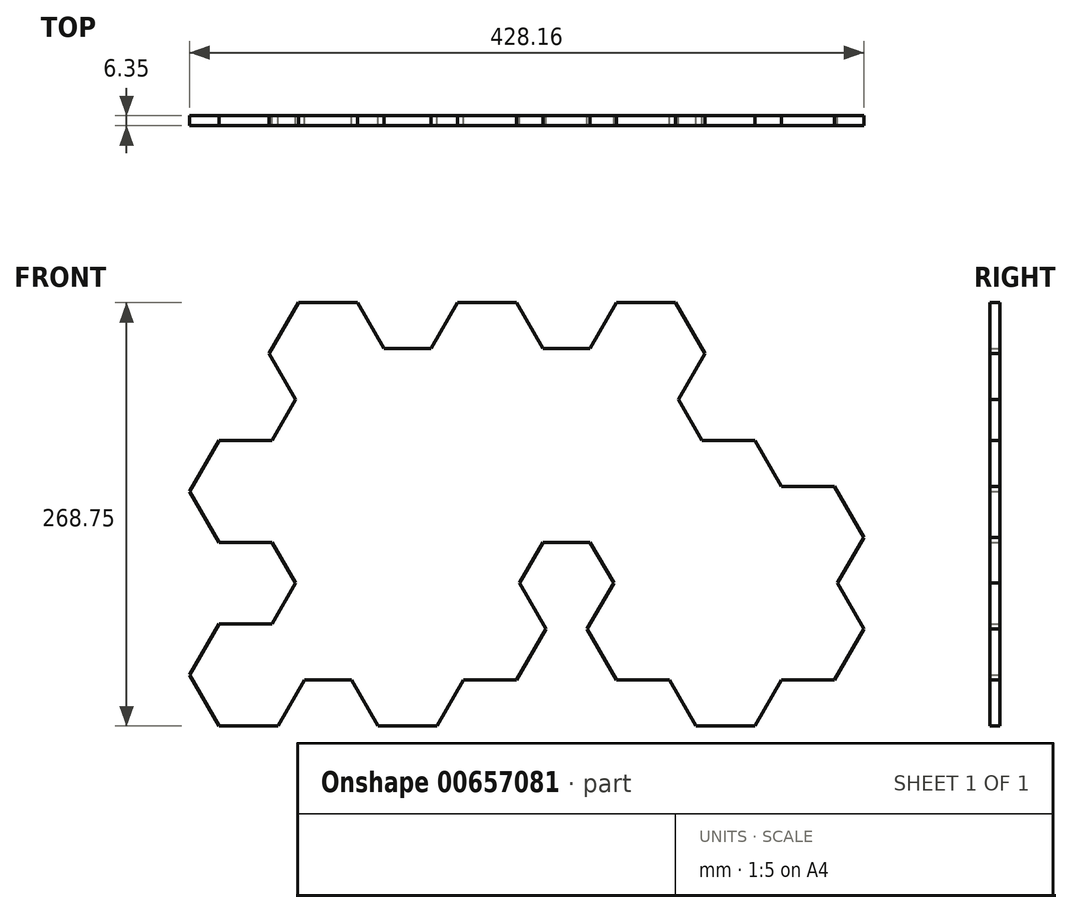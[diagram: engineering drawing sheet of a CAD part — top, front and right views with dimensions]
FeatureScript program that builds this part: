
annotation { "Feature Type Name" : "Feature", "Feature Type Description" : "" }
export const myFeature = defineFeature(function(context is Context, id is Id, definition is map)
    precondition{}
    {
        {
            var Q0;
            Q0=qCreatedBy(makeId("Front.planeOp"),FACE);
            var sketch = newSketch(context, id + "F0", { "sketchPlane" : qUnion([Q0])});
            skCircle(sketch, "E0.cCircle", {"center": v(-7.98, -23.48) * mm, "radius": 25.98 * mm, "construction": true});
            skLineSegment(sketch, "E0.0", {"start": v(22.02, -23.48) * mm, "end": v(7.02, -49.46) * mm});
            skLineSegment(sketch, "E0.1", {"start": v(7.02, -49.46) * mm, "end": v(-22.98, -49.46) * mm});
            skLineSegment(sketch, "E0.2", {"start": v(-22.98, -49.46) * mm, "end": v(-37.98, -23.48) * mm});
            skLineSegment(sketch, "E0.3", {"start": v(-37.98, -23.48) * mm, "end": v(-22.98, 2.5) * mm});
            skLineSegment(sketch, "E0.4", {"start": v(-22.98, 2.5) * mm, "end": v(7.02, 2.5) * mm});
            skLineSegment(sketch, "E0.5", {"start": v(7.02, 2.5) * mm, "end": v(22.02, -23.48) * mm});
            skPoint(sketch, "E0.0.midPoint", {"position": v(14.52, -36.47) * mm});
            skCircle(sketch, "E1.cCircle", {"center": v(-7.98, -81.8) * mm, "radius": 25.98 * mm, "construction": true});
            skLineSegment(sketch, "E1.0", {"start": v(22.02, -81.8) * mm, "end": v(7.02, -107.77) * mm});
            skLineSegment(sketch, "E1.1", {"start": v(7.02, -107.77) * mm, "end": v(-22.98, -107.77) * mm});
            skLineSegment(sketch, "E1.2", {"start": v(-22.98, -107.77) * mm, "end": v(-37.98, -81.8) * mm});
            skLineSegment(sketch, "E1.3", {"start": v(-37.98, -81.8) * mm, "end": v(-22.98, -55.81) * mm});
            skLineSegment(sketch, "E1.4", {"start": v(-22.98, -55.81) * mm, "end": v(7.02, -55.81) * mm});
            skLineSegment(sketch, "E1.5", {"start": v(7.02, -55.81) * mm, "end": v(22.02, -81.8) * mm});
            skPoint(sketch, "E1.0.midPoint", {"position": v(14.52, -94.78) * mm});
            skCircle(sketch, "E2.cCircle", {"center": v(-108.98, -81.8) * mm, "radius": 25.98 * mm, "construction": true});
            skLineSegment(sketch, "E2.0", {"start": v(-78.98, -81.8) * mm, "end": v(-93.98, -107.77) * mm});
            skLineSegment(sketch, "E2.1", {"start": v(-93.98, -107.77) * mm, "end": v(-123.98, -107.77) * mm});
            skLineSegment(sketch, "E2.2", {"start": v(-123.98, -107.77) * mm, "end": v(-138.98, -81.8) * mm});
            skLineSegment(sketch, "E2.3", {"start": v(-138.98, -81.8) * mm, "end": v(-123.98, -55.81) * mm});
            skLineSegment(sketch, "E2.4", {"start": v(-123.98, -55.81) * mm, "end": v(-93.98, -55.81) * mm});
            skLineSegment(sketch, "E2.5", {"start": v(-93.98, -55.81) * mm, "end": v(-78.98, -81.8) * mm});
            skPoint(sketch, "E2.0.midPoint", {"position": v(-86.48, -94.78) * mm});
            skCircle(sketch, "E3.cCircle", {"center": v(-108.98, -23.48) * mm, "radius": 25.98 * mm, "construction": true});
            skLineSegment(sketch, "E3.0", {"start": v(-78.98, -23.48) * mm, "end": v(-93.98, -49.46) * mm});
            skLineSegment(sketch, "E3.1", {"start": v(-93.98, -49.46) * mm, "end": v(-123.98, -49.46) * mm});
            skLineSegment(sketch, "E3.2", {"start": v(-123.98, -49.46) * mm, "end": v(-138.98, -23.48) * mm});
            skLineSegment(sketch, "E3.3", {"start": v(-138.98, -23.48) * mm, "end": v(-123.98, 2.5) * mm});
            skLineSegment(sketch, "E3.4", {"start": v(-123.98, 2.5) * mm, "end": v(-93.98, 2.5) * mm});
            skLineSegment(sketch, "E3.5", {"start": v(-93.98, 2.5) * mm, "end": v(-78.98, -23.48) * mm});
            skPoint(sketch, "E3.0.midPoint", {"position": v(-86.48, -36.47) * mm});
            skCircle(sketch, "E4.cCircle", {"center": v(-58.48, 5.67) * mm, "radius": 25.98 * mm, "construction": true});
            skLineSegment(sketch, "E4.0", {"start": v(-28.48, 5.67) * mm, "end": v(-43.48, -20.3) * mm});
            skLineSegment(sketch, "E4.1", {"start": v(-43.48, -20.3) * mm, "end": v(-73.48, -20.3) * mm});
            skLineSegment(sketch, "E4.2", {"start": v(-73.48, -20.3) * mm, "end": v(-88.48, 5.67) * mm});
            skLineSegment(sketch, "E4.3", {"start": v(-88.48, 5.67) * mm, "end": v(-73.48, 31.65) * mm});
            skLineSegment(sketch, "E4.4", {"start": v(-73.48, 31.65) * mm, "end": v(-43.48, 31.65) * mm});
            skLineSegment(sketch, "E4.5", {"start": v(-43.48, 31.65) * mm, "end": v(-28.48, 5.67) * mm});
            skPoint(sketch, "E4.0.midPoint", {"position": v(-35.98, -7.32) * mm});
            skCircle(sketch, "E5.cCircle", {"center": v(42.52, -110.95) * mm, "radius": 25.98 * mm, "construction": true});
            skLineSegment(sketch, "E5.0", {"start": v(72.52, -110.95) * mm, "end": v(57.52, -136.93) * mm});
            skLineSegment(sketch, "E5.1", {"start": v(57.52, -136.93) * mm, "end": v(27.52, -136.93) * mm});
            skLineSegment(sketch, "E5.2", {"start": v(27.52, -136.93) * mm, "end": v(12.52, -110.95) * mm});
            skLineSegment(sketch, "E5.3", {"start": v(12.52, -110.95) * mm, "end": v(27.52, -84.97) * mm});
            skLineSegment(sketch, "E5.4", {"start": v(27.52, -84.97) * mm, "end": v(57.52, -84.97) * mm});
            skLineSegment(sketch, "E5.5", {"start": v(57.52, -84.97) * mm, "end": v(72.52, -110.95) * mm});
            skPoint(sketch, "E5.0.midPoint", {"position": v(65.02, -123.94) * mm});
            skCircle(sketch, "E6.cCircle", {"center": v(-159.48, -110.95) * mm, "radius": 25.98 * mm, "construction": true});
            skLineSegment(sketch, "E6.0", {"start": v(-129.48, -110.95) * mm, "end": v(-144.48, -136.93) * mm});
            skLineSegment(sketch, "E6.1", {"start": v(-144.48, -136.93) * mm, "end": v(-174.48, -136.93) * mm});
            skLineSegment(sketch, "E6.2", {"start": v(-174.48, -136.93) * mm, "end": v(-189.48, -110.95) * mm});
            skLineSegment(sketch, "E6.3", {"start": v(-189.48, -110.95) * mm, "end": v(-174.48, -84.97) * mm});
            skLineSegment(sketch, "E6.4", {"start": v(-174.48, -84.97) * mm, "end": v(-144.48, -84.97) * mm});
            skLineSegment(sketch, "E6.5", {"start": v(-144.48, -84.97) * mm, "end": v(-129.48, -110.95) * mm});
            skPoint(sketch, "E6.0.midPoint", {"position": v(-136.98, -123.94) * mm});
            skCircle(sketch, "E7.cCircle", {"center": v(42.52, -52.64) * mm, "radius": 25.98 * mm, "construction": true});
            skLineSegment(sketch, "E7.0", {"start": v(72.52, -52.64) * mm, "end": v(57.52, -78.62) * mm});
            skLineSegment(sketch, "E7.1", {"start": v(57.52, -78.62) * mm, "end": v(27.52, -78.62) * mm});
            skLineSegment(sketch, "E7.2", {"start": v(27.52, -78.62) * mm, "end": v(12.52, -52.64) * mm});
            skLineSegment(sketch, "E7.3", {"start": v(12.52, -52.64) * mm, "end": v(27.52, -26.66) * mm});
            skLineSegment(sketch, "E7.4", {"start": v(27.52, -26.66) * mm, "end": v(57.52, -26.66) * mm});
            skLineSegment(sketch, "E7.5", {"start": v(57.52, -26.66) * mm, "end": v(72.52, -52.64) * mm});
            skPoint(sketch, "E7.0.midPoint", {"position": v(65.02, -65.63) * mm});
            skCircle(sketch, "E8.cCircle", {"center": v(93.02, -81.8) * mm, "radius": 25.98 * mm, "construction": true});
            skLineSegment(sketch, "E8.0", {"start": v(123.02, -81.8) * mm, "end": v(108.02, -107.77) * mm});
            skLineSegment(sketch, "E8.1", {"start": v(108.02, -107.77) * mm, "end": v(78.02, -107.77) * mm});
            skLineSegment(sketch, "E8.2", {"start": v(78.02, -107.77) * mm, "end": v(63.02, -81.8) * mm});
            skLineSegment(sketch, "E8.3", {"start": v(63.02, -81.8) * mm, "end": v(78.02, -55.81) * mm});
            skLineSegment(sketch, "E8.4", {"start": v(78.02, -55.81) * mm, "end": v(108.02, -55.81) * mm});
            skLineSegment(sketch, "E8.5", {"start": v(108.02, -55.81) * mm, "end": v(123.02, -81.8) * mm});
            skPoint(sketch, "E8.0.midPoint", {"position": v(115.52, -94.78) * mm});
            skCircle(sketch, "E9.cCircle", {"center": v(93.02, -23.48) * mm, "radius": 25.98 * mm, "construction": true});
            skLineSegment(sketch, "E9.0", {"start": v(123.02, -23.48) * mm, "end": v(108.02, -49.46) * mm});
            skLineSegment(sketch, "E9.1", {"start": v(108.02, -49.46) * mm, "end": v(78.02, -49.46) * mm});
            skLineSegment(sketch, "E9.2", {"start": v(78.02, -49.46) * mm, "end": v(63.02, -23.48) * mm});
            skLineSegment(sketch, "E9.3", {"start": v(63.02, -23.48) * mm, "end": v(78.02, 2.5) * mm});
            skLineSegment(sketch, "E9.4", {"start": v(78.02, 2.5) * mm, "end": v(108.02, 2.5) * mm});
            skLineSegment(sketch, "E9.5", {"start": v(108.02, 2.5) * mm, "end": v(123.02, -23.48) * mm});
            skPoint(sketch, "E9.0.midPoint", {"position": v(115.52, -36.47) * mm});
            skCircle(sketch, "E10.cCircle", {"center": v(42.52, 5.67) * mm, "radius": 25.98 * mm, "construction": true});
            skLineSegment(sketch, "E10.0", {"start": v(72.52, 5.67) * mm, "end": v(57.52, -20.3) * mm});
            skLineSegment(sketch, "E10.1", {"start": v(57.52, -20.3) * mm, "end": v(27.52, -20.3) * mm});
            skLineSegment(sketch, "E10.2", {"start": v(27.52, -20.3) * mm, "end": v(12.52, 5.67) * mm});
            skLineSegment(sketch, "E10.3", {"start": v(12.52, 5.67) * mm, "end": v(27.52, 31.65) * mm});
            skLineSegment(sketch, "E10.4", {"start": v(27.52, 31.65) * mm, "end": v(57.52, 31.65) * mm});
            skLineSegment(sketch, "E10.5", {"start": v(57.52, 31.65) * mm, "end": v(72.52, 5.67) * mm});
            skPoint(sketch, "E10.0.midPoint", {"position": v(65.02, -7.32) * mm});
            skCircle(sketch, "E11.cCircle", {"center": v(-7.98, 34.83) * mm, "radius": 25.98 * mm, "construction": true});
            skLineSegment(sketch, "E11.0", {"start": v(22.02, 34.83) * mm, "end": v(7.02, 8.85) * mm});
            skLineSegment(sketch, "E11.1", {"start": v(7.02, 8.85) * mm, "end": v(-22.98, 8.85) * mm});
            skLineSegment(sketch, "E11.2", {"start": v(-22.98, 8.85) * mm, "end": v(-37.98, 34.83) * mm});
            skLineSegment(sketch, "E11.3", {"start": v(-37.98, 34.83) * mm, "end": v(-22.98, 60.81) * mm});
            skLineSegment(sketch, "E11.4", {"start": v(-22.98, 60.81) * mm, "end": v(7.02, 60.81) * mm});
            skLineSegment(sketch, "E11.5", {"start": v(7.02, 60.81) * mm, "end": v(22.02, 34.83) * mm});
            skPoint(sketch, "E11.0.midPoint", {"position": v(14.52, 21.84) * mm});
            skCircle(sketch, "E12.cCircle", {"center": v(-7.98, 93.14) * mm, "radius": 25.98 * mm, "construction": true});
            skLineSegment(sketch, "E12.0", {"start": v(22.02, 93.14) * mm, "end": v(7.02, 67.16) * mm});
            skLineSegment(sketch, "E12.1", {"start": v(7.02, 67.16) * mm, "end": v(-22.98, 67.16) * mm});
            skLineSegment(sketch, "E12.2", {"start": v(-22.98, 67.16) * mm, "end": v(-37.98, 93.14) * mm});
            skLineSegment(sketch, "E12.3", {"start": v(-37.98, 93.14) * mm, "end": v(-22.98, 119.12) * mm});
            skLineSegment(sketch, "E12.4", {"start": v(-22.98, 119.12) * mm, "end": v(7.02, 119.12) * mm});
            skLineSegment(sketch, "E12.5", {"start": v(7.02, 119.12) * mm, "end": v(22.02, 93.14) * mm});
            skPoint(sketch, "E12.0.midPoint", {"position": v(14.52, 80.15) * mm});
            skCircle(sketch, "E13.cCircle", {"center": v(-58.48, 63.99) * mm, "radius": 25.98 * mm, "construction": true});
            skLineSegment(sketch, "E13.0", {"start": v(-28.48, 63.99) * mm, "end": v(-43.48, 38) * mm});
            skLineSegment(sketch, "E13.1", {"start": v(-43.48, 38) * mm, "end": v(-73.48, 38) * mm});
            skLineSegment(sketch, "E13.2", {"start": v(-73.48, 38) * mm, "end": v(-88.48, 63.99) * mm});
            skLineSegment(sketch, "E13.3", {"start": v(-88.48, 63.99) * mm, "end": v(-73.48, 89.97) * mm});
            skLineSegment(sketch, "E13.4", {"start": v(-73.48, 89.97) * mm, "end": v(-43.48, 89.97) * mm});
            skLineSegment(sketch, "E13.5", {"start": v(-43.48, 89.97) * mm, "end": v(-28.48, 63.99) * mm});
            skPoint(sketch, "E13.0.midPoint", {"position": v(-35.98, 51) * mm});
            skCircle(sketch, "E14.cCircle", {"center": v(-108.98, 34.83) * mm, "radius": 25.98 * mm, "construction": true});
            skLineSegment(sketch, "E14.0", {"start": v(-78.98, 34.83) * mm, "end": v(-93.98, 8.85) * mm});
            skLineSegment(sketch, "E14.1", {"start": v(-93.98, 8.85) * mm, "end": v(-123.98, 8.85) * mm});
            skLineSegment(sketch, "E14.2", {"start": v(-123.98, 8.85) * mm, "end": v(-138.98, 34.83) * mm});
            skLineSegment(sketch, "E14.3", {"start": v(-138.98, 34.83) * mm, "end": v(-123.98, 60.81) * mm});
            skLineSegment(sketch, "E14.4", {"start": v(-123.98, 60.81) * mm, "end": v(-93.98, 60.81) * mm});
            skLineSegment(sketch, "E14.5", {"start": v(-93.98, 60.81) * mm, "end": v(-78.98, 34.83) * mm});
            skPoint(sketch, "E14.0.midPoint", {"position": v(-86.48, 21.84) * mm});
            skCircle(sketch, "E15.cCircle", {"center": v(-108.98, 93.14) * mm, "radius": 25.98 * mm, "construction": true});
            skLineSegment(sketch, "E15.0", {"start": v(-78.98, 93.14) * mm, "end": v(-93.98, 67.16) * mm});
            skLineSegment(sketch, "E15.1", {"start": v(-93.98, 67.16) * mm, "end": v(-123.98, 67.16) * mm});
            skLineSegment(sketch, "E15.2", {"start": v(-123.98, 67.16) * mm, "end": v(-138.98, 93.14) * mm});
            skLineSegment(sketch, "E15.3", {"start": v(-138.98, 93.14) * mm, "end": v(-123.98, 119.12) * mm});
            skLineSegment(sketch, "E15.4", {"start": v(-123.98, 119.12) * mm, "end": v(-93.98, 119.12) * mm});
            skLineSegment(sketch, "E15.5", {"start": v(-93.98, 119.12) * mm, "end": v(-78.98, 93.14) * mm});
            skPoint(sketch, "E15.0.midPoint", {"position": v(-86.48, 80.15) * mm});
            skCircle(sketch, "E16.cCircle", {"center": v(-159.48, 63.99) * mm, "radius": 25.98 * mm, "construction": true});
            skLineSegment(sketch, "E16.0", {"start": v(-129.48, 63.99) * mm, "end": v(-144.48, 38) * mm});
            skLineSegment(sketch, "E16.1", {"start": v(-144.48, 38) * mm, "end": v(-174.48, 38) * mm});
            skLineSegment(sketch, "E16.2", {"start": v(-174.48, 38) * mm, "end": v(-189.48, 63.99) * mm});
            skLineSegment(sketch, "E16.3", {"start": v(-189.48, 63.99) * mm, "end": v(-174.48, 89.97) * mm});
            skLineSegment(sketch, "E16.4", {"start": v(-174.48, 89.97) * mm, "end": v(-144.48, 89.97) * mm});
            skLineSegment(sketch, "E16.5", {"start": v(-144.48, 89.97) * mm, "end": v(-129.48, 63.99) * mm});
            skPoint(sketch, "E16.0.midPoint", {"position": v(-136.98, 51) * mm});
            skCircle(sketch, "E17.cCircle", {"center": v(-159.48, 5.67) * mm, "radius": 25.98 * mm, "construction": true});
            skLineSegment(sketch, "E17.0", {"start": v(-129.48, 5.67) * mm, "end": v(-144.48, -20.3) * mm});
            skLineSegment(sketch, "E17.1", {"start": v(-144.48, -20.3) * mm, "end": v(-174.48, -20.3) * mm});
            skLineSegment(sketch, "E17.2", {"start": v(-174.48, -20.3) * mm, "end": v(-189.48, 5.67) * mm});
            skLineSegment(sketch, "E17.3", {"start": v(-189.48, 5.67) * mm, "end": v(-174.48, 31.65) * mm});
            skLineSegment(sketch, "E17.4", {"start": v(-174.48, 31.65) * mm, "end": v(-144.48, 31.65) * mm});
            skLineSegment(sketch, "E17.5", {"start": v(-144.48, 31.65) * mm, "end": v(-129.48, 5.67) * mm});
            skPoint(sketch, "E17.0.midPoint", {"position": v(-136.98, -7.32) * mm});
            skCircle(sketch, "E18.cCircle", {"center": v(-159.48, -52.64) * mm, "radius": 25.98 * mm, "construction": true});
            skLineSegment(sketch, "E18.0", {"start": v(-129.48, -52.64) * mm, "end": v(-144.48, -78.62) * mm});
            skLineSegment(sketch, "E18.1", {"start": v(-144.48, -78.62) * mm, "end": v(-174.48, -78.62) * mm});
            skLineSegment(sketch, "E18.2", {"start": v(-174.48, -78.62) * mm, "end": v(-189.48, -52.64) * mm});
            skLineSegment(sketch, "E18.3", {"start": v(-189.48, -52.64) * mm, "end": v(-174.48, -26.66) * mm});
            skLineSegment(sketch, "E18.4", {"start": v(-174.48, -26.66) * mm, "end": v(-144.48, -26.66) * mm});
            skLineSegment(sketch, "E18.5", {"start": v(-144.48, -26.66) * mm, "end": v(-129.48, -52.64) * mm});
            skPoint(sketch, "E18.0.midPoint", {"position": v(-136.98, -65.63) * mm});
            skCircle(sketch, "E19.cCircle", {"center": v(-209.98, -81.8) * mm, "radius": 25.98 * mm, "construction": true});
            skLineSegment(sketch, "E19.0", {"start": v(-179.98, -81.8) * mm, "end": v(-194.98, -107.77) * mm});
            skLineSegment(sketch, "E19.1", {"start": v(-194.98, -107.77) * mm, "end": v(-224.98, -107.77) * mm});
            skLineSegment(sketch, "E19.2", {"start": v(-224.98, -107.77) * mm, "end": v(-239.98, -81.8) * mm});
            skLineSegment(sketch, "E19.3", {"start": v(-239.98, -81.8) * mm, "end": v(-224.98, -55.81) * mm});
            skLineSegment(sketch, "E19.4", {"start": v(-224.98, -55.81) * mm, "end": v(-194.98, -55.81) * mm});
            skLineSegment(sketch, "E19.5", {"start": v(-194.98, -55.81) * mm, "end": v(-179.98, -81.8) * mm});
            skPoint(sketch, "E19.0.midPoint", {"position": v(-187.48, -94.78) * mm});
            skCircle(sketch, "E20.cCircle", {"center": v(-209.98, -23.48) * mm, "radius": 25.98 * mm, "construction": true});
            skLineSegment(sketch, "E20.0", {"start": v(-179.98, -23.48) * mm, "end": v(-194.98, -49.46) * mm});
            skLineSegment(sketch, "E20.1", {"start": v(-194.98, -49.46) * mm, "end": v(-224.98, -49.46) * mm});
            skLineSegment(sketch, "E20.2", {"start": v(-224.98, -49.46) * mm, "end": v(-239.98, -23.48) * mm});
            skLineSegment(sketch, "E20.3", {"start": v(-239.98, -23.48) * mm, "end": v(-224.98, 2.5) * mm});
            skLineSegment(sketch, "E20.4", {"start": v(-224.98, 2.5) * mm, "end": v(-194.98, 2.5) * mm});
            skLineSegment(sketch, "E20.5", {"start": v(-194.98, 2.5) * mm, "end": v(-179.98, -23.48) * mm});
            skPoint(sketch, "E20.0.midPoint", {"position": v(-187.48, -36.47) * mm});
            skCircle(sketch, "E21.cCircle", {"center": v(-209.98, 34.83) * mm, "radius": 25.98 * mm, "construction": true});
            skLineSegment(sketch, "E21.0", {"start": v(-179.98, 34.83) * mm, "end": v(-194.98, 8.85) * mm});
            skLineSegment(sketch, "E21.1", {"start": v(-194.98, 8.85) * mm, "end": v(-224.98, 8.85) * mm});
            skLineSegment(sketch, "E21.2", {"start": v(-224.98, 8.85) * mm, "end": v(-239.98, 34.83) * mm});
            skLineSegment(sketch, "E21.3", {"start": v(-239.98, 34.83) * mm, "end": v(-224.98, 60.81) * mm});
            skLineSegment(sketch, "E21.4", {"start": v(-224.98, 60.81) * mm, "end": v(-194.98, 60.81) * mm});
            skLineSegment(sketch, "E21.5", {"start": v(-194.98, 60.81) * mm, "end": v(-179.98, 34.83) * mm});
            skPoint(sketch, "E21.0.midPoint", {"position": v(-187.48, 21.84) * mm});
            skCircle(sketch, "E22.cCircle", {"center": v(-209.98, 93.14) * mm, "radius": 25.98 * mm, "construction": true});
            skLineSegment(sketch, "E22.0", {"start": v(-179.98, 93.14) * mm, "end": v(-194.98, 67.16) * mm});
            skLineSegment(sketch, "E22.1", {"start": v(-194.98, 67.16) * mm, "end": v(-224.98, 67.16) * mm});
            skLineSegment(sketch, "E22.2", {"start": v(-224.98, 67.16) * mm, "end": v(-239.98, 93.14) * mm});
            skLineSegment(sketch, "E22.3", {"start": v(-239.98, 93.14) * mm, "end": v(-224.98, 119.12) * mm});
            skLineSegment(sketch, "E22.4", {"start": v(-224.98, 119.12) * mm, "end": v(-194.98, 119.12) * mm});
            skLineSegment(sketch, "E22.5", {"start": v(-194.98, 119.12) * mm, "end": v(-179.98, 93.14) * mm});
            skPoint(sketch, "E22.0.midPoint", {"position": v(-187.48, 80.15) * mm});
            skCircle(sketch, "E23.cCircle", {"center": v(-260.48, 5.67) * mm, "radius": 25.98 * mm, "construction": true});
            skLineSegment(sketch, "E23.0", {"start": v(-230.48, 5.67) * mm, "end": v(-245.48, -20.3) * mm});
            skLineSegment(sketch, "E23.1", {"start": v(-245.48, -20.3) * mm, "end": v(-275.48, -20.3) * mm});
            skLineSegment(sketch, "E23.2", {"start": v(-275.48, -20.3) * mm, "end": v(-290.48, 5.67) * mm});
            skLineSegment(sketch, "E23.3", {"start": v(-290.48, 5.67) * mm, "end": v(-275.48, 31.65) * mm});
            skLineSegment(sketch, "E23.4", {"start": v(-275.48, 31.65) * mm, "end": v(-245.48, 31.65) * mm});
            skLineSegment(sketch, "E23.5", {"start": v(-245.48, 31.65) * mm, "end": v(-230.48, 5.67) * mm});
            skPoint(sketch, "E23.0.midPoint", {"position": v(-237.98, -7.32) * mm});
            skCircle(sketch, "E24.cCircle", {"center": v(-260.48, -110.95) * mm, "radius": 25.98 * mm, "construction": true});
            skLineSegment(sketch, "E24.0", {"start": v(-230.48, -110.95) * mm, "end": v(-245.48, -136.93) * mm});
            skLineSegment(sketch, "E24.1", {"start": v(-245.48, -136.93) * mm, "end": v(-275.48, -136.93) * mm});
            skLineSegment(sketch, "E24.2", {"start": v(-275.48, -136.93) * mm, "end": v(-290.48, -110.95) * mm});
            skLineSegment(sketch, "E24.3", {"start": v(-290.48, -110.95) * mm, "end": v(-275.48, -84.97) * mm});
            skLineSegment(sketch, "E24.4", {"start": v(-275.48, -84.97) * mm, "end": v(-245.48, -84.97) * mm});
            skLineSegment(sketch, "E24.5", {"start": v(-245.48, -84.97) * mm, "end": v(-230.48, -110.95) * mm});
            skPoint(sketch, "E24.0.midPoint", {"position": v(-237.98, -123.94) * mm});
            skLineSegment(sketch, "E25", {"start": v(-123.98, -114.12) * mm, "end": v(-140.81, -143.28) * mm});
            skLineSegment(sketch, "E26", {"start": v(-90.32, -114.12) * mm, "end": v(-71.65, -81.8) * mm});
            skLineSegment(sketch, "E27", {"start": v(-71.65, -81.8) * mm, "end": v(-88.48, -52.64) * mm});
            skLineSegment(sketch, "E28", {"start": v(-88.48, -52.64) * mm, "end": v(-73.48, -26.66) * mm});
            skLineSegment(sketch, "E29", {"start": v(-73.48, -26.66) * mm, "end": v(-43.48, -26.66) * mm});
            skLineSegment(sketch, "E30", {"start": v(-45.32, -81.8) * mm, "end": v(-26.65, -114.12) * mm});
            skLineSegment(sketch, "E31", {"start": v(-26.65, -114.12) * mm, "end": v(7.02, -114.12) * mm});
            skLineSegment(sketch, "E32", {"start": v(7.02, -114.12) * mm, "end": v(23.85, -143.28) * mm});
            skLineSegment(sketch, "E33", {"start": v(23.85, -143.28) * mm, "end": v(61.18, -143.28) * mm});
            skLineSegment(sketch, "E34", {"start": v(61.18, -143.28) * mm, "end": v(78.02, -114.12) * mm});
            skLineSegment(sketch, "E35", {"start": v(78.02, -114.12) * mm, "end": v(111.68, -114.12) * mm});
            skLineSegment(sketch, "E36", {"start": v(111.68, -114.12) * mm, "end": v(130.35, -81.8) * mm});
            skLineSegment(sketch, "E37", {"start": v(130.35, -81.8) * mm, "end": v(113.51, -52.64) * mm});
            skLineSegment(sketch, "E38", {"start": v(113.51, -52.64) * mm, "end": v(130.35, -23.48) * mm});
            skLineSegment(sketch, "E39", {"start": v(130.35, -23.48) * mm, "end": v(111.68, 8.85) * mm});
            skLineSegment(sketch, "E40", {"start": v(111.68, 8.85) * mm, "end": v(78.02, 8.85) * mm});
            skLineSegment(sketch, "E41", {"start": v(78.02, 8.85) * mm, "end": v(61.18, 38) * mm});
            skLineSegment(sketch, "E42", {"start": v(61.18, 38) * mm, "end": v(27.52, 38) * mm});
            skLineSegment(sketch, "E43", {"start": v(27.52, 38) * mm, "end": v(12.52, 63.99) * mm});
            skLineSegment(sketch, "E44", {"start": v(12.52, 63.99) * mm, "end": v(29.35, 93.14) * mm});
            skLineSegment(sketch, "E45", {"start": v(29.35, 93.14) * mm, "end": v(10.68, 125.47) * mm});
            skLineSegment(sketch, "E46", {"start": v(10.68, 125.47) * mm, "end": v(-26.65, 125.47) * mm});
            skLineSegment(sketch, "E47", {"start": v(-26.65, 125.47) * mm, "end": v(-43.48, 96.32) * mm});
            skLineSegment(sketch, "E48", {"start": v(-43.48, 96.32) * mm, "end": v(-73.48, 96.32) * mm});
            skLineSegment(sketch, "E49", {"start": v(-73.48, 96.32) * mm, "end": v(-90.32, 125.47) * mm});
            skLineSegment(sketch, "E50", {"start": v(-90.32, 125.47) * mm, "end": v(-127.65, 125.47) * mm});
            skLineSegment(sketch, "E51", {"start": v(-144.48, 96.32) * mm, "end": v(-127.65, 125.47) * mm});
            skLineSegment(sketch, "E52", {"start": v(-144.48, 96.32) * mm, "end": v(-174.48, 96.32) * mm});
            skLineSegment(sketch, "E53", {"start": v(-174.48, 96.32) * mm, "end": v(-191.31, 125.47) * mm});
            skLineSegment(sketch, "E54", {"start": v(-191.31, 125.47) * mm, "end": v(-228.65, 125.47) * mm});
            skLineSegment(sketch, "E55", {"start": v(-228.65, 125.47) * mm, "end": v(-247.31, 93.14) * mm});
            skLineSegment(sketch, "E56", {"start": v(-247.31, 93.14) * mm, "end": v(-230.48, 63.99) * mm});
            skLineSegment(sketch, "E57", {"start": v(-230.48, 63.99) * mm, "end": v(-245.48, 38) * mm});
            skLineSegment(sketch, "E58", {"start": v(-245.48, 38) * mm, "end": v(-279.15, 38) * mm});
            skLineSegment(sketch, "E59", {"start": v(-279.15, 38) * mm, "end": v(-297.81, 5.67) * mm});
            skLineSegment(sketch, "E60", {"start": v(-297.81, 5.67) * mm, "end": v(-279.15, -26.66) * mm});
            skLineSegment(sketch, "E61", {"start": v(-279.15, -26.66) * mm, "end": v(-245.48, -26.66) * mm});
            skLineSegment(sketch, "E62", {"start": v(-245.48, -26.66) * mm, "end": v(-230.48, -52.64) * mm});
            skLineSegment(sketch, "E63", {"start": v(-230.48, -52.64) * mm, "end": v(-245.48, -78.62) * mm});
            skLineSegment(sketch, "E64", {"start": v(-245.48, -78.62) * mm, "end": v(-279.15, -78.62) * mm});
            skLineSegment(sketch, "E65", {"start": v(-279.15, -78.62) * mm, "end": v(-297.81, -110.95) * mm});
            skLineSegment(sketch, "E66", {"start": v(-297.81, -110.95) * mm, "end": v(-279.15, -143.28) * mm});
            skLineSegment(sketch, "E67", {"start": v(-279.15, -143.28) * mm, "end": v(-241.81, -143.28) * mm});
            skLineSegment(sketch, "E68", {"start": v(-241.81, -143.28) * mm, "end": v(-224.98, -114.12) * mm});
            skLineSegment(sketch, "E69", {"start": v(-224.98, -114.12) * mm, "end": v(-194.98, -114.12) * mm});
            skLineSegment(sketch, "E70", {"start": v(-194.98, -114.12) * mm, "end": v(-178.15, -143.28) * mm});
            skLineSegment(sketch, "E71", {"start": v(-178.15, -143.28) * mm, "end": v(-140.81, -143.28) * mm});
            skLineSegment(sketch, "E72", {"start": v(-43.48, -26.66) * mm, "end": v(-28.48, -52.64) * mm});
            skLineSegment(sketch, "E73", {"start": v(-28.48, -52.64) * mm, "end": v(-45.32, -81.8) * mm});
            skLineSegment(sketch, "E74", {"start": v(-90.32, -114.12) * mm, "end": v(-123.98, -114.12) * mm});
            skSolve(sketch);
        }
        {
            var Q0;
            Q0=qSketchRegion(id+"F0",true);
            var Q1;
            Q1=makeQuery(id+"F0.imprint","IMPRINT",FACE,{"disambiguationData":[TD([[makeQuery(id+"F0.imprint","IMPRINT",EDGE,{"derivedFrom":sQuery(id+"F0.wireOp",EDGE,"E22.0")}),-1.0]])]});
            var Q2;
            Q2=makeQuery(id+"F0.imprint","IMPRINT",FACE,{"disambiguationData":[TD([[makeQuery(id+"F0.imprint","IMPRINT",EDGE,{"derivedFrom":sQuery(id+"F0.wireOp",EDGE,"E21.0")}),-1.0]])]});
            var Q3;
            Q3=makeQuery(id+"F0.imprint","IMPRINT",FACE,{"disambiguationData":[TD([[makeQuery(id+"F0.imprint","IMPRINT",EDGE,{"derivedFrom":sQuery(id+"F0.wireOp",EDGE,"E16.0")}),-1.0]])]});
            var Q4;
            Q4=makeQuery(id+"F0.imprint","IMPRINT",FACE,{"disambiguationData":[TD([[makeQuery(id+"F0.imprint","IMPRINT",EDGE,{"derivedFrom":sQuery(id+"F0.wireOp",EDGE,"E15.0")}),-1.0]])]});
            var Q5;
            Q5=makeQuery(id+"F0.imprint","IMPRINT",FACE,{"disambiguationData":[TD([[makeQuery(id+"F0.imprint","IMPRINT",EDGE,{"derivedFrom":sQuery(id+"F0.wireOp",EDGE,"E14.0")}),-1.0]])]});
            var Q6;
            Q6=makeQuery(id+"F0.imprint","IMPRINT",FACE,{"disambiguationData":[TD([[makeQuery(id+"F0.imprint","IMPRINT",EDGE,{"derivedFrom":sQuery(id+"F0.wireOp",EDGE,"E17.0")}),-1.0]])]});
            var Q7;
            Q7=makeQuery(id+"F0.imprint","IMPRINT",FACE,{"disambiguationData":[TD([[makeQuery(id+"F0.imprint","IMPRINT",EDGE,{"derivedFrom":sQuery(id+"F0.wireOp",EDGE,"E20.0")}),-1.0]])]});
            var Q8;
            Q8=makeQuery(id+"F0.imprint","IMPRINT",FACE,{"disambiguationData":[TD([[makeQuery(id+"F0.imprint","IMPRINT",EDGE,{"derivedFrom":sQuery(id+"F0.wireOp",EDGE,"E19.0")}),-1.0]])]});
            var Q9;
            Q9=makeQuery(id+"F0.imprint","IMPRINT",FACE,{"disambiguationData":[TD([[makeQuery(id+"F0.imprint","IMPRINT",EDGE,{"derivedFrom":sQuery(id+"F0.wireOp",EDGE,"E6.0")}),-1.0]])]});
            var Q10;
            Q10=makeQuery(id+"F0.imprint","IMPRINT",FACE,{"disambiguationData":[TD([[makeQuery(id+"F0.imprint","IMPRINT",EDGE,{"derivedFrom":sQuery(id+"F0.wireOp",EDGE,"E18.0")}),-1.0]])]});
            var Q11;
            Q11=makeQuery(id+"F0.imprint","IMPRINT",FACE,{"disambiguationData":[TD([[makeQuery(id+"F0.imprint","IMPRINT",EDGE,{"derivedFrom":sQuery(id+"F0.wireOp",EDGE,"E2.0")}),-1.0]])]});
            var Q12;
            Q12=makeQuery(id+"F0.imprint","IMPRINT",FACE,{"disambiguationData":[TD([[makeQuery(id+"F0.imprint","IMPRINT",EDGE,{"derivedFrom":sQuery(id+"F0.wireOp",EDGE,"E4.0")}),-1.0]])]});
            var Q13;
            Q13=makeQuery(id+"F0.imprint","IMPRINT",FACE,{"disambiguationData":[TD([[makeQuery(id+"F0.imprint","IMPRINT",EDGE,{"derivedFrom":sQuery(id+"F0.wireOp",EDGE,"E11.0")}),-1.0]])]});
            var Q14;
            Q14=makeQuery(id+"F0.imprint","IMPRINT",FACE,{"disambiguationData":[TD([[makeQuery(id+"F0.imprint","IMPRINT",EDGE,{"derivedFrom":sQuery(id+"F0.wireOp",EDGE,"E12.0")}),-1.0]])]});
            var Q15;
            Q15=makeQuery(id+"F0.imprint","IMPRINT",FACE,{"disambiguationData":[TD([[makeQuery(id+"F0.imprint","IMPRINT",EDGE,{"derivedFrom":sQuery(id+"F0.wireOp",EDGE,"E10.0")}),-1.0]])]});
            var Q16;
            Q16=makeQuery(id+"F0.imprint","IMPRINT",FACE,{"disambiguationData":[TD([[makeQuery(id+"F0.imprint","IMPRINT",EDGE,{"derivedFrom":sQuery(id+"F0.wireOp",EDGE,"E1.0")}),-1.0]])]});
            var Q17;
            Q17=makeQuery(id+"F0.imprint","IMPRINT",FACE,{"disambiguationData":[TD([[makeQuery(id+"F0.imprint","IMPRINT",EDGE,{"derivedFrom":sQuery(id+"F0.wireOp",EDGE,"E7.0")}),-1.0]])]});
            var Q18;
            Q18=makeQuery(id+"F0.imprint","IMPRINT",FACE,{"disambiguationData":[TD([[makeQuery(id+"F0.imprint","IMPRINT",EDGE,{"derivedFrom":sQuery(id+"F0.wireOp",EDGE,"E9.0")}),-1.0]])]});
            var Q19;
            Q19=makeQuery(id+"F0.imprint","IMPRINT",FACE,{"disambiguationData":[TD([[makeQuery(id+"F0.imprint","IMPRINT",EDGE,{"derivedFrom":sQuery(id+"F0.wireOp",EDGE,"E8.0")}),-1.0]])]});
            var Q20;
            Q20=makeQuery(id+"F0.imprint","IMPRINT",FACE,{"disambiguationData":[TD([[makeQuery(id+"F0.imprint","IMPRINT",EDGE,{"derivedFrom":sQuery(id+"F0.wireOp",EDGE,"E5.0")}),-1.0]])]});
            var Q21;
            Q21=makeQuery(id+"F0.imprint","IMPRINT",FACE,{"disambiguationData":[TD([[makeQuery(id+"F0.imprint","IMPRINT",EDGE,{"derivedFrom":sQuery(id+"F0.wireOp",EDGE,"E23.0")}),-1.0]])]});
            var Q22;
            Q22=makeQuery(id+"F0.imprint","IMPRINT",FACE,{"disambiguationData":[TD([[makeQuery(id+"F0.imprint","IMPRINT",EDGE,{"derivedFrom":sQuery(id+"F0.wireOp",EDGE,"E3.0")}),-1.0]])]});
            var Q23;
            Q23=makeQuery(id+"F0.imprint","IMPRINT",FACE,{"disambiguationData":[TD([[makeQuery(id+"F0.imprint","IMPRINT",EDGE,{"derivedFrom":sQuery(id+"F0.wireOp",EDGE,"E13.0")}),-1.0]])]});
            var Q24;
            Q24=makeQuery(id+"F0.imprint","IMPRINT",FACE,{"disambiguationData":[TD([[makeQuery(id+"F0.imprint","IMPRINT",EDGE,{"derivedFrom":sQuery(id+"F0.wireOp",EDGE,"E0.0")}),-1.0]])]});
            var Q25;
            Q25=makeQuery(id+"F0.imprint","IMPRINT",FACE,{"disambiguationData":[TD([[makeQuery(id+"F0.imprint","IMPRINT",EDGE,{"derivedFrom":sQuery(id+"F0.wireOp",EDGE,"E24.0")}),-1.0]])]});
            extrude(context, id + "F1", {"entities" : qUnion([Q0, Q1, Q2, Q3, Q4, Q5, Q6, Q7, Q8, Q9, Q10, Q11, Q12, Q13, Q14, Q15, Q16, Q17, Q18, Q19, Q20, Q21, Q22, Q23, Q24, Q25]), "depth" : 6.35 * mm, "offsetDistance" : 25.4 * mm});
        }
    });
